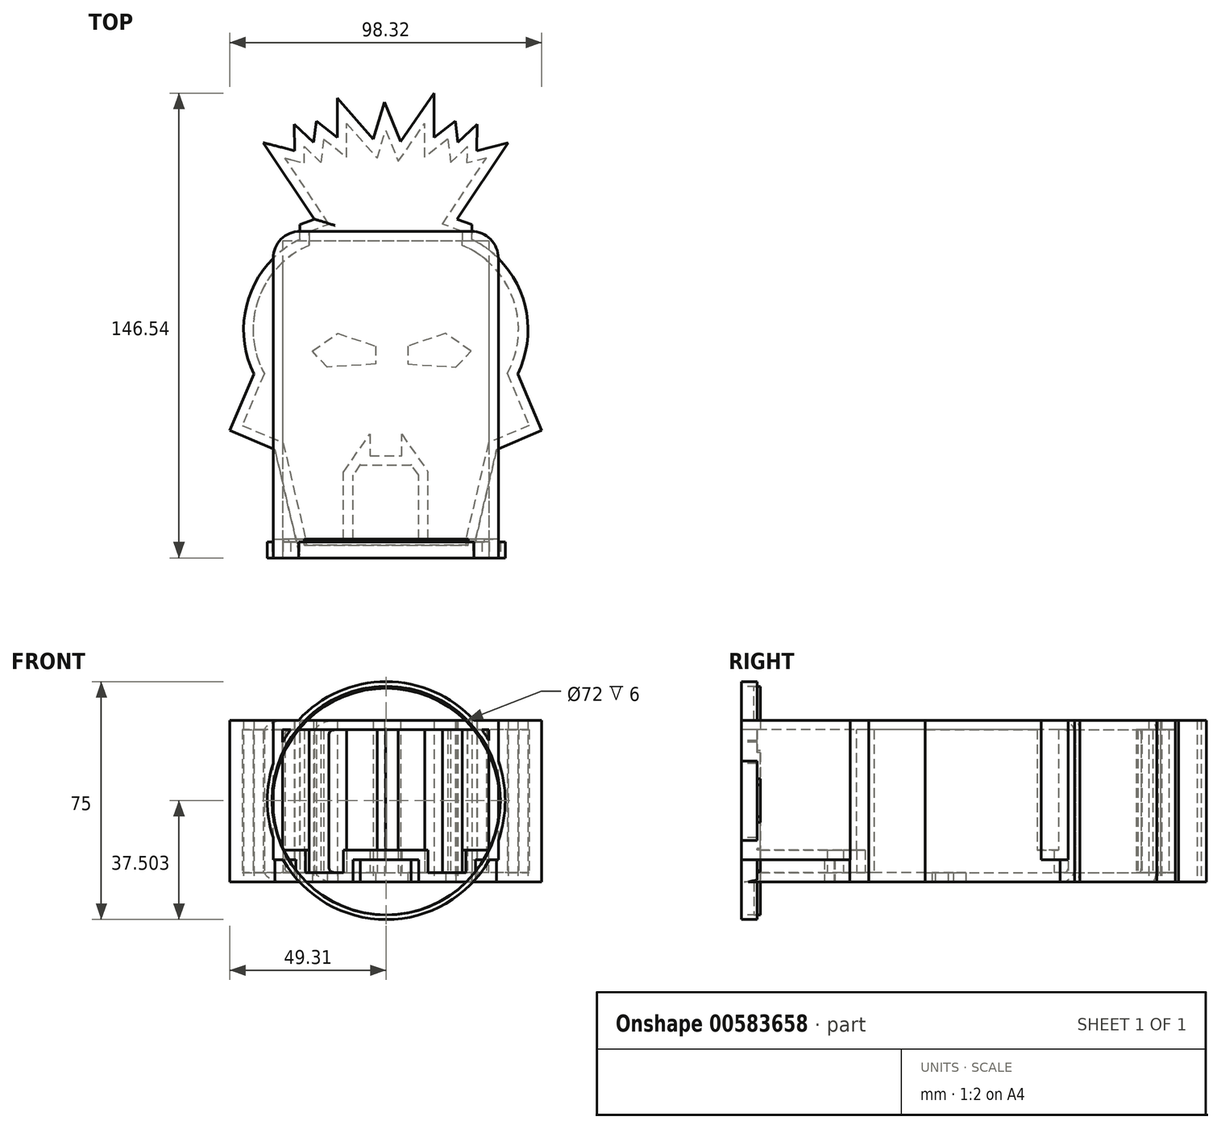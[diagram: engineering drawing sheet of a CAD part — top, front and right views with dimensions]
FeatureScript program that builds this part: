
annotation { "Feature Type Name" : "Feature", "Feature Type Description" : "" }
export const myFeature = defineFeature(function(context is Context, id is Id, definition is map)
    precondition{}
    {
        {
            var Q0;
            Q0=qCreatedBy(makeId("Top.planeOp"),FACE);
            var sketch = newSketch(context, id + "F0", { "sketchPlane" : qUnion([Q0])});
            skLineSegment(sketch, "E0", {"start": v(-38.3, -12.71) * mm, "end": v(-45.23, -29.07) * mm});
            skLineSegment(sketch, "E1", {"start": v(-45.23, -29.07) * mm, "end": v(-32.38, -34.51) * mm});
            skLineSegment(sketch, "E2", {"start": v(-32.38, -34.51) * mm, "end": v(-23.85, -70.83) * mm});
            skLineSegment(sketch, "E3", {"start": v(-23.85, -70.83) * mm, "end": v(-13.34, -70.83) * mm});
            skLineSegment(sketch, "E4", {"start": v(-13.34, -70.83) * mm, "end": v(-13.34, -43.75) * mm});
            skLineSegment(sketch, "E5", {"start": v(-13.34, -43.75) * mm, "end": v(-5, -31.79) * mm});
            skLineSegment(sketch, "E6", {"start": v(-5, -31.79) * mm, "end": v(-5, -38.64) * mm});
            skLineSegment(sketch, "E7", {"start": v(-5, -38.64) * mm, "end": v(0, -38.64) * mm});
            skLineSegment(sketch, "E8", {"start": v(-17.87, 34.44) * mm, "end": v(-31.74, 55.24) * mm});
            skLineSegment(sketch, "E9", {"start": v(-24.11, 32.15) * mm, "end": v(-17.87, 34.44) * mm});
            skLineSegment(sketch, "E10", {"start": v(-25.74, 58.87) * mm, "end": v(-20.48, 53.84) * mm});
            skLineSegment(sketch, "E11", {"start": v(-12.28, 55.5) * mm, "end": v(-12.28, 66.16) * mm});
            skLineSegment(sketch, "E12", {"start": v(-12.28, 66.16) * mm, "end": v(-2.75, 55.24) * mm});
            skLineSegment(sketch, "E13", {"start": v(-2.75, 55.24) * mm, "end": v(0, 64) * mm});
            skLineSegment(sketch, "E14", {"start": v(-19.56, 61.27) * mm, "end": v(-12.28, 55.5) * mm});
            skLineSegment(sketch, "E15", {"start": v(-19.56, 61.27) * mm, "end": v(-20.48, 53.84) * mm});
            skArc(sketch, "E16", {"start": v(-24.11, 27.73) * mm, "mid": v(-40.2, 10.66) * mm, "end": v(-38.3, -12.71) * mm});
            skLineSegment(sketch, "E17", {"start": v(-31.74, 55.24) * mm, "end": v(-25.67, 53.67) * mm});
            skLineSegment(sketch, "E18", {"start": v(-25.67, 53.67) * mm, "end": v(-25.74, 58.87) * mm});
            skLineSegment(sketch, "E19", {"start": v(0, 79.09) * mm, "end": v(0, -69.65) * mm, "construction": true});
            skLineSegment(sketch, "E20.MirrorCS", {"start": v(25.67, 53.67) * mm, "end": v(25.74, 58.87) * mm});
            skLineSegment(sketch, "E21.MirrorCS", {"start": v(19.56, 61.27) * mm, "end": v(20.48, 53.84) * mm});
            skLineSegment(sketch, "E22.MirrorCS", {"start": v(19.56, 61.27) * mm, "end": v(12.28, 55.5) * mm});
            skLineSegment(sketch, "E23.MirrorCS", {"start": v(12.28, 55.5) * mm, "end": v(12.28, 66.16) * mm});
            skLineSegment(sketch, "E24.MirrorCS", {"start": v(25.74, 58.87) * mm, "end": v(20.48, 53.84) * mm});
            skLineSegment(sketch, "E25.MirrorCS", {"start": v(31.74, 55.24) * mm, "end": v(25.67, 53.67) * mm});
            skLineSegment(sketch, "E26.MirrorCS", {"start": v(24.11, 32.15) * mm, "end": v(17.87, 34.44) * mm});
            skLineSegment(sketch, "E27.MirrorCS", {"start": v(23.85, -70.83) * mm, "end": v(13.34, -70.83) * mm});
            skLineSegment(sketch, "E28.MirrorCS", {"start": v(32.38, -34.51) * mm, "end": v(23.85, -70.83) * mm});
            skLineSegment(sketch, "E29.MirrorCS", {"start": v(17.87, 34.44) * mm, "end": v(31.74, 55.24) * mm});
            skLineSegment(sketch, "E30.MirrorCS", {"start": v(13.34, -70.83) * mm, "end": v(13.34, -43.75) * mm});
            skLineSegment(sketch, "E31.MirrorCS", {"start": v(45.23, -29.07) * mm, "end": v(32.38, -34.51) * mm});
            skLineSegment(sketch, "E32.MirrorCS", {"start": v(38.3, -12.71) * mm, "end": v(45.23, -29.07) * mm});
            skArc(sketch, "E33.MirrorCS", {"start": v(24.11, 27.73) * mm, "mid": v(40.2, 10.66) * mm, "end": v(38.3, -12.71) * mm});
            skLineSegment(sketch, "E34", {"start": v(0, 64) * mm, "end": v(3.95, 54.2) * mm});
            skLineSegment(sketch, "E35", {"start": v(3.95, 54.2) * mm, "end": v(12.28, 66.16) * mm});
            skLineSegment(sketch, "E36", {"start": v(0, -38.64) * mm, "end": v(5, -38.64) * mm});
            skLineSegment(sketch, "E37", {"start": v(5, -38.64) * mm, "end": v(5, -31.79) * mm});
            skLineSegment(sketch, "E38", {"start": v(5, -31.79) * mm, "end": v(13.34, -43.75) * mm});
            skLineSegment(sketch, "E39", {"start": v(-24.11, 32.15) * mm, "end": v(-24.11, 27.73) * mm});
            skLineSegment(sketch, "E40", {"start": v(24.11, 32.15) * mm, "end": v(24.11, 27.73) * mm});
            skSolve(sketch);
        }
        {
            var Q0;
            Q0=qSketchRegion(id+"F0",true);
            extrude(context, id + "F1", {"entities" : qUnion([Q0]), "depth" : 45 * mm, "offsetDistance" : 25 * mm});
        }
        {
            var Q0;
            Q0=qCreatedBy(makeId("Top.planeOp"),FACE);
            var sketch = newSketch(context, id + "F2", { "sketchPlane" : qUnion([Q0])});
            skLineSegment(sketch, "E41", {"start": v(-23.16, -5.6) * mm, "end": v(-18.41, -10.67) * mm});
            skLineSegment(sketch, "E42", {"start": v(-18.41, -10.67) * mm, "end": v(-3.2, -9.69) * mm});
            skLineSegment(sketch, "E43", {"start": v(-3.2, -9.69) * mm, "end": v(-3.2, -4.02) * mm});
            skLineSegment(sketch, "E44", {"start": v(-3.2, -4.02) * mm, "end": v(-15.14, 0) * mm});
            skLineSegment(sketch, "E45", {"start": v(-15.14, 0) * mm, "end": v(-23.16, -5.6) * mm});
            skLineSegment(sketch, "E46", {"start": v(-15.14, 0) * mm, "end": v(-10.75, -1.03) * mm});
            skFitSpline(sketch, "E47", {"points": [v(-10.75, -1.03) * mm, v(-10.75, 2.44) * mm, v(-12.29, 3.2) * mm, v(-11.11, 6.02) * mm], "startDerivative": vector(-4.83, 8.14) * mm, "endDerivative": vector(5.33, 8.63) * mm});
            skLineSegment(sketch, "E48", {"start": v(1.86, -15.53) * mm, "end": v(1.86, 7.72) * mm, "construction": true});
            skLineSegment(sketch, "E49.MirrorCS", {"start": v(6.93, -9.69) * mm, "end": v(6.93, -4.02) * mm});
            skLineSegment(sketch, "E50.MirrorCS", {"start": v(22.13, -10.67) * mm, "end": v(6.93, -9.69) * mm});
            skLineSegment(sketch, "E51.MirrorCS", {"start": v(6.93, -4.02) * mm, "end": v(18.86, 0) * mm});
            skLineSegment(sketch, "E52.MirrorCS", {"start": v(26.88, -5.6) * mm, "end": v(22.13, -10.67) * mm});
            skLineSegment(sketch, "E53.MirrorCS", {"start": v(18.86, 0) * mm, "end": v(26.88, -5.6) * mm});
            skLineSegment(sketch, "E54.MirrorCS", {"start": v(18.86, 0) * mm, "end": v(14.47, -1.03) * mm});
            skFitSpline(sketch, "E55.MirrorCS", {"points": [v(14.47, -1.03) * mm, v(14.47, 2.44) * mm, v(16, 3.2) * mm, v(14.84, 6.02) * mm], "startDerivative": vector(4.83, 8.14) * mm, "endDerivative": vector(-5.33, 8.63) * mm});
            skPoint(sketch, "E56", {"position": v(1.86, 13.91) * mm});
            skSolve(sketch);
        }
        {
            var Q0;
            Q0=makeQuery(id+"F1.opExtrude","CAP_EDGE",EDGE,{"disambiguationData":[OSD([sQuery(id+"F0.wireOp",EDGE,"QlBGKe7W-CjFm-zpKe-syDU-rIZYVbdessFk")])],"isStart":false});
            var Q1;
            Q1=makeQuery(id+"F1.opExtrude","CAP_EDGE",EDGE,{"disambiguationData":[OSD([sQuery(id+"F0.wireOp",EDGE,"E210.MirrorCS")])],"isStart":false});
            var Q2;
            Q2=makeQuery(id+"F1.opExtrude","CAP_EDGE",EDGE,{"disambiguationData":[OSD([sQuery(id+"F0.wireOp",EDGE,"E9")])],"isStart":false});
            var Q3;
            Q3=makeQuery(id+"F1.opExtrude","CAP_EDGE",EDGE,{"disambiguationData":[OSD([sQuery(id+"F0.wireOp",EDGE,"E26.MirrorCS")])],"isStart":false});
            fillet(context, id + "F3", {"entities" : qUnion([Q0, Q1, Q2, Q3]), "radius" : 1.02 * mm, "tangentPropagation" : true, "allowEdgeOverflow" : false});
        }
        {
            var Q0;
            Q0=makeQuery(id+"F3.opFillet","BLEND_EDGE",EDGE,{"blendedFrom":[makeQuery(id+"F1.opExtrude","CAP_EDGE",EDGE,{"disambiguationData":[OSD([sQuery(id+"F0.wireOp",EDGE,"E9")])],"isStart":false}),makeQuery(id+"F1.opExtrude","CAP_EDGE",EDGE,{"disambiguationData":[OSD([sQuery(id+"F0.wireOp",EDGE,"QlBGKe7W-CjFm-zpKe-syDU-rIZYVbdessFk")])],"isStart":false})],"blendedInto":[]});
            var Q1;
            Q1=makeQuery(id+"F3.opFillet","BLEND_EDGE",EDGE,{"blendedFrom":[makeQuery(id+"F1.opExtrude","CAP_EDGE",EDGE,{"disambiguationData":[OSD([sQuery(id+"F0.wireOp",EDGE,"E26.MirrorCS")])],"isStart":false}),makeQuery(id+"F1.opExtrude","CAP_EDGE",EDGE,{"disambiguationData":[OSD([sQuery(id+"F0.wireOp",EDGE,"E210.MirrorCS")])],"isStart":false})],"blendedInto":[]});
            var Q2;
            Q2=makeQuery(id+"F1.opExtrude","CAP_EDGE",EDGE,{"disambiguationData":[OSD([sQuery(id+"F0.wireOp",EDGE,"E8")])],"isStart":false});
            var Q3;
            Q3=makeQuery(id+"F1.opExtrude","CAP_EDGE",EDGE,{"disambiguationData":[OSD([sQuery(id+"F0.wireOp",EDGE,"E29.MirrorCS")])],"isStart":false});
            var Q4;
            Q4=makeQuery(id+"F1.opExtrude","CAP_EDGE",EDGE,{"disambiguationData":[OSD([sQuery(id+"F0.wireOp",EDGE,"E8")])],"isStart":true});
            var Q5;
            Q5=makeQuery(id+"F1.opExtrude","CAP_EDGE",EDGE,{"disambiguationData":[OSD([sQuery(id+"F0.wireOp",EDGE,"E29.MirrorCS")])],"isStart":true});
            var Q6;
            Q6=makeQuery(id+"F1.opExtrude","CAP_EDGE",EDGE,{"disambiguationData":[OSD([sQuery(id+"F0.wireOp",EDGE,"E26.MirrorCS")])],"isStart":true});
            var Q7;
            Q7=makeQuery(id+"F1.opExtrude","CAP_EDGE",EDGE,{"disambiguationData":[OSD([sQuery(id+"F0.wireOp",EDGE,"E210.MirrorCS")])],"isStart":true});
            var Q8;
            Q8=makeQuery(id+"F1.opExtrude","CAP_EDGE",EDGE,{"disambiguationData":[OSD([sQuery(id+"F0.wireOp",EDGE,"QlBGKe7W-CjFm-zpKe-syDU-rIZYVbdessFk")])],"isStart":true});
            var Q9;
            Q9=makeQuery(id+"F1.opExtrude","CAP_EDGE",EDGE,{"disambiguationData":[OSD([sQuery(id+"F0.wireOp",EDGE,"E9")])],"isStart":true});
            fillet(context, id + "F4", {"entities" : qUnion([Q0, Q1, Q2, Q3, Q4, Q5, Q6, Q7, Q8, Q9]), "radius" : 1.27 * mm, "tangentPropagation" : true, "allowEdgeOverflow" : false});
        }
        {
            var Q0;
            Q0=makeQuery(id+"F1.opExtrude","CAP_FACE",FACE,{"disambiguationData":[OSD([sQuery(id+"F0.wireOp",EDGE,"E0"),sQuery(id+"F0.wireOp",EDGE,"E1"),sQuery(id+"F0.wireOp",EDGE,"E2"),sQuery(id+"F0.wireOp",EDGE,"E3"),sQuery(id+"F0.wireOp",EDGE,"E4"),sQuery(id+"F0.wireOp",EDGE,"E5"),sQuery(id+"F0.wireOp",EDGE,"E6"),sQuery(id+"F0.wireOp",EDGE,"E7"),sQuery(id+"F0.wireOp",EDGE,"QlBGKe7W-CjFm-zpKe-syDU-rIZYVbdessFk"),sQuery(id+"F0.wireOp",EDGE,"E8"),sQuery(id+"F0.wireOp",EDGE,"E9"),sQuery(id+"F0.wireOp",EDGE,"E10"),sQuery(id+"F0.wireOp",EDGE,"E11"),sQuery(id+"F0.wireOp",EDGE,"YeJSSkTn-FtL6-i8Rl-ahXc-JzPqReOcuTEl"),sQuery(id+"F0.wireOp",EDGE,"0AvRNHQZ-9jO7-RX2F-YmTK-DABBuAo3s7oE"),sQuery(id+"F0.wireOp",EDGE,"xWFMa1az-Kvkm-zQS0-EvPk-zAxefn89ps1X"),sQuery(id+"F0.wireOp",EDGE,"PtLbIQZY-IS9e-ehaK-3uLq-SwewusbjE9fL"),sQuery(id+"F0.wireOp",EDGE,"E12"),sQuery(id+"F0.wireOp",EDGE,"E13"),sQuery(id+"F0.wireOp",EDGE,"E14"),sQuery(id+"F0.wireOp",EDGE,"E15"),sQuery(id+"F0.wireOp",EDGE,"E16"),sQuery(id+"F0.wireOp",EDGE,"E17"),sQuery(id+"F0.wireOp",EDGE,"E18"),sQuery(id+"F0.wireOp",EDGE,"E20.MirrorCS"),sQuery(id+"F0.wireOp",EDGE,"E21.MirrorCS"),sQuery(id+"F0.wireOp",EDGE,"E22.MirrorCS"),sQuery(id+"F0.wireOp",EDGE,"E23.MirrorCS"),sQuery(id+"F0.wireOp",EDGE,"E24.MirrorCS"),sQuery(id+"F0.wireOp",EDGE,"8db37806-3d3e-4eaf-9e43-167e2250198d6.MirrorCS"),sQuery(id+"F0.wireOp",EDGE,"8db37806-3d3e-4eaf-9e43-167e2250198d8.MirrorCS"),sQuery(id+"F0.wireOp",EDGE,"E210.MirrorCS"),sQuery(id+"F0.wireOp",EDGE,"E26.MirrorCS"),sQuery(id+"F0.wireOp",EDGE,"E27.MirrorCS"),sQuery(id+"F0.wireOp",EDGE,"E25.MirrorCS"),sQuery(id+"F0.wireOp",EDGE,"83e56f64-14f1-453a-9d83-025f2e8a94ae3.MirrorCS"),sQuery(id+"F0.wireOp",EDGE,"E31.MirrorCS"),sQuery(id+"F0.wireOp",EDGE,"E29.MirrorCS"),sQuery(id+"F0.wireOp",EDGE,"E30.MirrorCS"),sQuery(id+"F0.wireOp",EDGE,"E28.MirrorCS"),sQuery(id+"F0.wireOp",EDGE,"E32.MirrorCS"),sQuery(id+"F0.wireOp",EDGE,"E33.MirrorCS"),sQuery(id+"F0.wireOp",EDGE,"E34"),sQuery(id+"F0.wireOp",EDGE,"E35"),sQuery(id+"F0.wireOp",EDGE,"KlBAluSZ-iXYF-gunQ-GgUj-j9AXwpjWbuxS"),sQuery(id+"F0.wireOp",EDGE,"E36"),sQuery(id+"F0.wireOp",EDGE,"E37"),sQuery(id+"F0.wireOp",EDGE,"E38")])],"isStart":true});
            var sketch = newSketch(context, id + "F5", { "sketchPlane" : qUnion([Q0])});
            skLineSegment(sketch, "E57", {"start": v(15.92, -33.8) * mm, "end": v(-15.92, -33.8) * mm});
            skSolve(sketch);
        }
        {
            var Q0;
            Q0=qSketchRegion(id+"F5",true);
            var Q1;
            Q1=sQuery(id+"F5.wireOp",EDGE,"E57");
            extrude(context, id + "F6", {"entities" : qUnion([Q0]), "bodyType" : ToolBodyType.SURFACE, "operationType" : NewBodyOperationType.REMOVE, "surfaceEntities" : qUnion([Q1]), "oppositeDirection" : true, "depth" : 0.25 * mm});
        }
        {
            var Q0;
            Q0=makeQuery(id+"F1.opExtrude","SWEPT_FACE",FACE,{"disambiguationData":[OSD([sQuery(id+"F0.wireOp",EDGE,"E3")])]});
            var sketch = newSketch(context, id + "F7", { "sketchPlane" : qUnion([Q0])});
            skCircle(sketch, "E58", {"center": v(-13.34, 22.5) * mm, "radius": 37.5 * mm});
            skLineSegment(sketch, "E59", {"start": v(-13.34, 22.5) * mm, "end": v(13.87, 22.5) * mm});
            skSolve(sketch);
        }
        {
            var Q0;
            Q0=makeQuery(id+"F7.imprint","IMPRINT",FACE,{"disambiguationData":[TD([[makeQuery(id+"F7.imprint","IMPRINT",EDGE,{"derivedFrom":sQuery(id+"F7.wireOp",EDGE,"E58")}),1.0]])]});
            var sketch = newSketch(context, id + "F8", { "sketchPlane" : qUnion([Q0])});
            skLineSegment(sketch, "E60.bottom", {"start": v(-32.5, 45.03) * mm, "end": v(32.5, 45.03) * mm});
            skLineSegment(sketch, "E60.top", {"start": v(-32.5, 7.03) * mm, "end": v(32.5, 7.03) * mm});
            skLineSegment(sketch, "E60.left", {"start": v(-32.5, 45.03) * mm, "end": v(-32.5, 7.03) * mm});
            skLineSegment(sketch, "E60.right", {"start": v(32.5, 45.03) * mm, "end": v(32.5, 7.03) * mm});
            skSolve(sketch);
        }
        {
            var Q0;
            Q0=qSketchRegion(id+"F8",true);
            extrude(context, id + "F9", {"entities" : qUnion([Q0]), "operationType" : NewBodyOperationType.ADD, "oppositeDirection" : true, "depth" : 100 * mm, "offsetDistance" : 25 * mm});
        }
        {
            var Q0;
            Q0=makeQuery(id+"F9.boolean.opBoolean","MERGE",FACE,{"derivedFrom":[makeQuery(id+"F1.opExtrude","SWEPT_FACE",FACE,{"disambiguationData":[OSD([sQuery(id+"F0.wireOp",EDGE,"E3")])]}),makeQuery(id+"F1.opExtrude","SWEPT_FACE",FACE,{"disambiguationData":[OSD([sQuery(id+"F0.wireOp",EDGE,"E27.MirrorCS")])]}),makeQuery(id+"F9.opExtrude","CAP_FACE",FACE,{"disambiguationData":[OSD([sQuery(id+"F8.wireOp",EDGE,"E60.bottom"),sQuery(id+"F8.wireOp",EDGE,"E60.top"),sQuery(id+"F8.wireOp",EDGE,"E60.left"),sQuery(id+"F8.wireOp",EDGE,"E60.right")])],"isStart":true})]});
            shell(context, id + "F10", {"entities" : qUnion([Q0]), "thickness" : 3 * mm, "oppositeDirection" : true});
        }
        {
            var Q0;
            Q0=makeQuery(id+"F9.opExtrude","CAP_EDGE",EDGE,{"disambiguationData":[OSD([sQuery(id+"F8.wireOp",EDGE,"E60.left")])],"isStart":false});
            var Q1;
            Q1=makeQuery(id+"F9.opExtrude","CAP_EDGE",EDGE,{"disambiguationData":[OSD([sQuery(id+"F8.wireOp",EDGE,"E60.right")])],"isStart":false});
            fillet(context, id + "F11", {"entities" : qUnion([Q0, Q1]), "radius" : 8.5 * mm, "tangentPropagation" : true, "allowEdgeOverflow" : false});
        }
        {
            var Q0;
            Q0=qSketchRegion(id+"F2",true);
            extrude(context, id + "F12", {"entities" : qUnion([Q0]), "operationType" : NewBodyOperationType.REMOVE, "endBound" : BoundingType.SYMMETRIC, "depth" : 10 * mm, "offsetDistance" : 25 * mm});
        }
        {
            var Q0;
            Q0=makeQuery(id+"F7.imprint","IMPRINT",FACE,{"disambiguationData":[TD([[makeQuery(id+"F7.imprint","IMPRINT",EDGE,{"derivedFrom":sQuery(id+"F7.wireOp",EDGE,"E58")}),1.0]])]});
            var sketch = newSketch(context, id + "F13", { "sketchPlane" : qUnion([Q0])});
            skCircle(sketch, "E61", {"center": v(0.15, 22.7) * mm, "radius": 37.5 * mm});
            skSolve(sketch);
        }
        {
            var Q0;
            Q0=qSketchRegion(id+"F13",true);
            extrude(context, id + "F14", {"entities" : qUnion([Q0]), "operationType" : NewBodyOperationType.ADD, "oppositeDirection" : true, "depth" : 5 * mm, "offsetDistance" : 25 * mm});
        }
        {
            var Q0;
            Q0=makeQuery(id+"F14.boolean.opBoolean","MERGE",FACE,{"derivedFrom":[makeQuery(id+"F9.boolean.opBoolean","MERGE",FACE,{"derivedFrom":[makeQuery(id+"F1.opExtrude","SWEPT_FACE",FACE,{"disambiguationData":[OSD([sQuery(id+"F0.wireOp",EDGE,"E3")])]}),makeQuery(id+"F1.opExtrude","SWEPT_FACE",FACE,{"disambiguationData":[OSD([sQuery(id+"F0.wireOp",EDGE,"E27.MirrorCS")])]}),makeQuery(id+"F9.opExtrude","CAP_FACE",FACE,{"disambiguationData":[OSD([sQuery(id+"F8.wireOp",EDGE,"E60.bottom"),sQuery(id+"F8.wireOp",EDGE,"E60.top"),sQuery(id+"F8.wireOp",EDGE,"E60.left"),sQuery(id+"F8.wireOp",EDGE,"E60.right")])],"isStart":true})]}),makeQuery(id+"F14.opExtrude","CAP_FACE",FACE,{"disambiguationData":[OSD([sQuery(id+"F13.wireOp",EDGE,"E61")])],"isStart":true})]});
            var sketch = newSketch(context, id + "F15", { "sketchPlane" : qUnion([Q0])});
            skCircle(sketch, "E62", {"center": v(0.15, 22.7) * mm, "radius": 36 * mm});
            skSolve(sketch);
        }
        {
            var Q0;
            Q0=qSketchRegion(id+"F15",true);
            extrude(context, id + "F16", {"entities" : qUnion([Q0]), "operationType" : NewBodyOperationType.REMOVE, "oppositeDirection" : true, "depth" : 6 * mm, "offsetDistance" : 25 * mm});
        }
        {
            var Q0;
            {var subQ47=sQuery(id+"F0.wireOp",EDGE,"E2");var subQ52=makeQuery(id+"F1.opExtrude","SWEPT_FACE",FACE,{"disambiguationData":[OSD([subQ47])]});var subQ53=sQuery(id+"F15.wireOp",EDGE,"E62");Q0=makeQuery(id+"F16.boolean.opBoolean","COPY",FACE,{"disambiguationData":[TD([subQ52])],"derivedFrom":makeQuery(id+"F16.opExtrude","CAP_FACE",FACE,{"disambiguationData":[OSD([subQ53])],"isStart":false})});}
            var sketch = newSketch(context, id + "F17", { "sketchPlane" : qUnion([Q0])});
            skLineSegment(sketch, "E63", {"start": v(-25.07, -3) * mm, "end": v(25.37, -3) * mm});
            skArc(sketch, "E64", {"start": v(-25.07, -3) * mm, "mid": v(0.15, -13.41) * mm, "end": v(25.37, -3) * mm});
            skLineSegment(sketch, "E65", {"start": v(-25.67, 48.03) * mm, "end": v(26, 48.03) * mm});
            skArc(sketch, "E66", {"start": v(26, 48.03) * mm, "mid": v(0.17, 58.66) * mm, "end": v(-25.67, 48.03) * mm});
            skSolve(sketch);
        }
        {
            var Q0;
            Q0=qSketchRegion(id+"F17",true);
            extrude(context, id + "F18", {"entities" : qUnion([Q0]), "depth" : 2 * mm, "offsetDistance" : 25 * mm});
        }
    });
